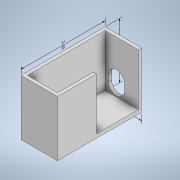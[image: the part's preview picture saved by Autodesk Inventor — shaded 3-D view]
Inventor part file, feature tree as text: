
AUTODESK INVENTOR PART (.ipt)
format: ipt  version: 2020 (Build 240168000, 168)  size: 143,872 bytes
history: native  units: in
note: dims shown in document units (in); Inventor stores cm internally (conversion verified against a paired STEP export)
features: other x4, extrude x3, sketch x3, fillet x1
ambient origin geometry x8: Origin, YZ Plane, XZ Plane, XY Plane, X Axis, Y Axis, Z Axis, Center Point
bodies: Solid1 (feature_tree)
feature tree (11):
  other  "Annotations"
  extrude  "Extrusion1"  Depth=2.6in
  extrude  "Extrusion2"  Depth=0.1in
  extrude  "Extrusion3"  Depth=0.1in
  fillet  "Fillet1"  Radius=0.1in
  sketch  "Sketch1"  dims[d0=1.13in d1=2.6in]
  sketch  "Sketch2"  dims[d2=0.12in d3=0.0in d4=0.1in]
  sketch  "Sketch3"  dims[d5=0.1in d6=0.1in d7=0.1in d8=1.1in d9=1.6in d10=0.0in d11=0.2in d12=0.15in d13=0.5in d14=0.7in d15=0.1in d16=0.0in d17=0.25in d18=0.0372in d19=0.1118in d20=1.72in d21=0.0in d22=0.3937in d23=1.13in d24=0.0in d25=0.3937in d26=2.6in]
  other  "Linear Dimension 1"
  other  "Linear Dimension 2"
  other  "Linear Dimension 3"
